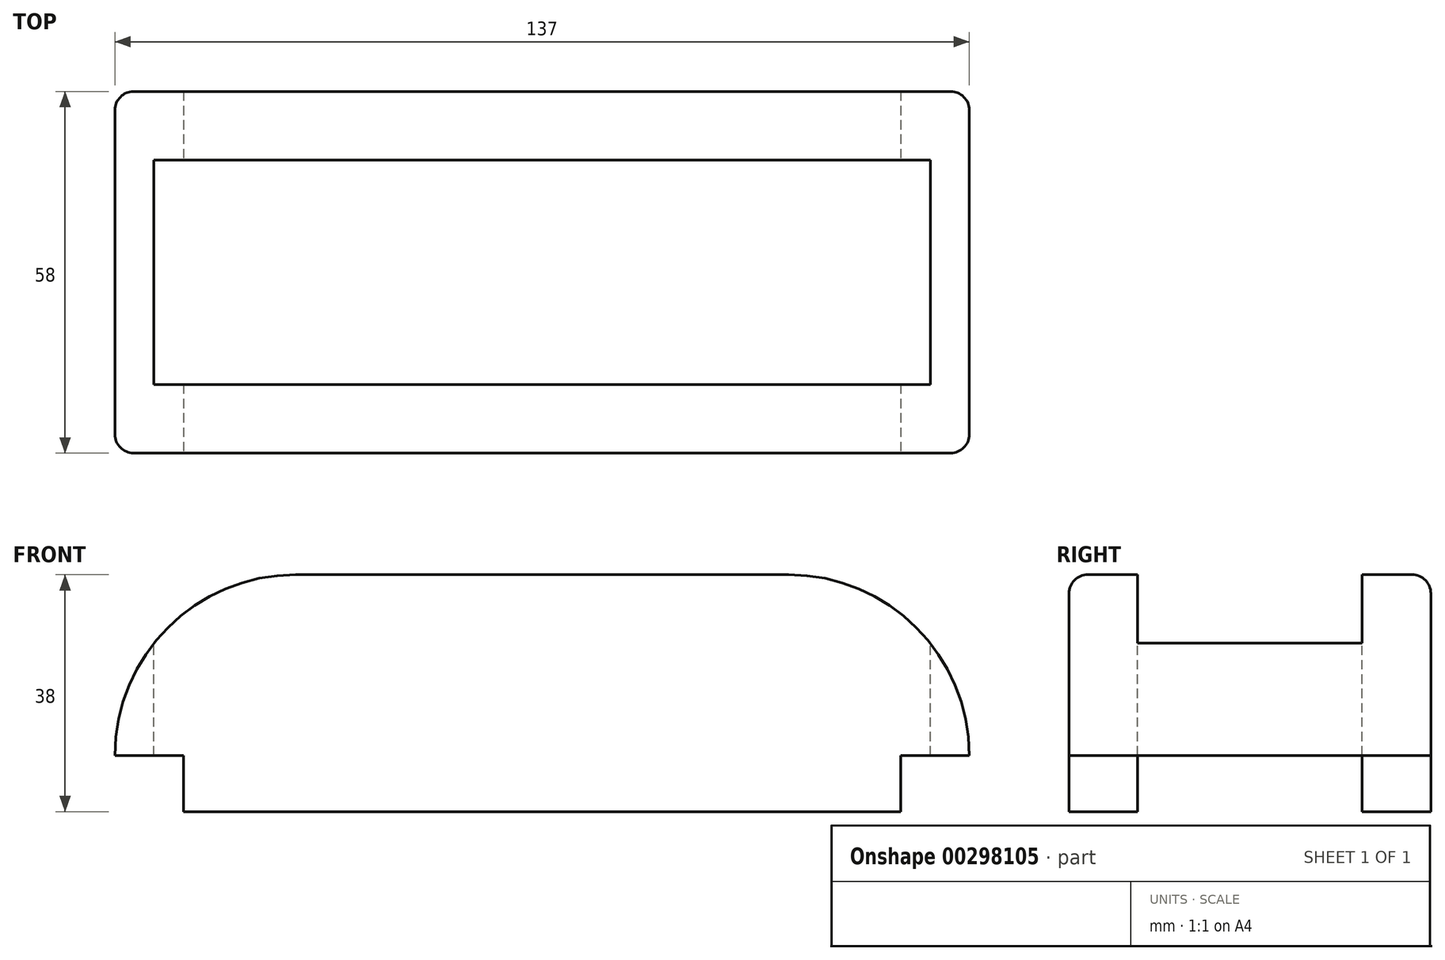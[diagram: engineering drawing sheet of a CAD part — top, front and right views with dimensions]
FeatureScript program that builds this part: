
annotation { "Feature Type Name" : "Feature", "Feature Type Description" : "" }
export const myFeature = defineFeature(function(context is Context, id is Id, definition is map)
    precondition{}
    {
        {
            var Q0;
            Q0=qCreatedBy(makeId("Front.planeOp"),FACE);
            var sketch = newSketch(context, id + "F0", { "sketchPlane" : qUnion([Q0])});
            skLineSegment(sketch, "E0.bottom", {"start": v(0, 0) * mm, "end": v(137, 0) * mm});
            skLineSegment(sketch, "E0.top", {"start": v(0, -38) * mm, "end": v(137, -38) * mm});
            skLineSegment(sketch, "E0.left", {"start": v(0, 0) * mm, "end": v(0, -38) * mm});
            skLineSegment(sketch, "E0.right", {"start": v(137, 0) * mm, "end": v(137, -38) * mm});
            skSolve(sketch);
        }
        {
            var Q0;
            Q0=makeQuery(id+"F0.imprint","IMPRINT",FACE,{"disambiguationData":[TD([[makeQuery(id+"F0.imprint","IMPRINT",EDGE,{"derivedFrom":sQuery(id+"F0.wireOp",EDGE,"E0.bottom")}),-1.0]])]});
            extrude(context, id + "F1", {"entities" : qUnion([Q0]), "depth" : 58 * mm});
        }
        {
            var Q0;
            Q0=makeQuery(id+"F1.opExtrude","CAP_FACE",FACE,{"disambiguationData":[OSD([sQuery(id+"F0.wireOp",EDGE,"E0.bottom"),sQuery(id+"F0.wireOp",EDGE,"E0.top"),sQuery(id+"F0.wireOp",EDGE,"E0.left"),sQuery(id+"F0.wireOp",EDGE,"E0.right")])],"isStart":false});
            var sketch = newSketch(context, id + "F2", { "sketchPlane" : qUnion([Q0])});
            skLineSegment(sketch, "E1.bottom", {"start": v(137, -38) * mm, "end": v(126, -38) * mm});
            skLineSegment(sketch, "E1.top", {"start": v(137, -29) * mm, "end": v(126, -29) * mm});
            skLineSegment(sketch, "E1.left", {"start": v(137, -38) * mm, "end": v(137, -29) * mm});
            skLineSegment(sketch, "E1.right", {"start": v(126, -38) * mm, "end": v(126, -29) * mm});
            skLineSegment(sketch, "E2.bottom", {"start": v(0, -38) * mm, "end": v(11, -38) * mm});
            skLineSegment(sketch, "E2.top", {"start": v(0, -29) * mm, "end": v(11, -29) * mm});
            skLineSegment(sketch, "E2.left", {"start": v(0, -38) * mm, "end": v(0, -29) * mm});
            skLineSegment(sketch, "E2.right", {"start": v(11, -38) * mm, "end": v(11, -29) * mm});
            skSolve(sketch);
        }
        {
            var Q0;
            Q0=makeQuery(id+"F2.imprint","IMPRINT",FACE,{"disambiguationData":[TD([[makeQuery(id+"F2.imprint","IMPRINT",EDGE,{"derivedFrom":sQuery(id+"F2.wireOp",EDGE,"E1.bottom")}),1.0]])]});
            var Q1;
            Q1=makeQuery(id+"F2.imprint","IMPRINT",FACE,{"disambiguationData":[TD([[makeQuery(id+"F2.imprint","IMPRINT",EDGE,{"derivedFrom":sQuery(id+"F2.wireOp",EDGE,"E2.bottom")}),1.0]])]});
            extrude(context, id + "F3", {"entities" : qUnion([Q0, Q1]), "operationType" : NewBodyOperationType.REMOVE, "endBound" : BoundingType.THROUGH_ALL, "oppositeDirection" : true, "depth" : 25 * mm});
        }
        {
            var Q0;
            Q0=makeQuery(id+"F1.opExtrude","SWEPT_EDGE",EDGE,{"disambiguationData":[OSD([sQuery(id+"F0.wireOp",EDGE,"E0.bottom"),sQuery(id+"F0.wireOp",EDGE,"E0.left")])]});
            var Q1;
            Q1=makeQuery(id+"F1.opExtrude","SWEPT_EDGE",EDGE,{"disambiguationData":[OSD([sQuery(id+"F0.wireOp",EDGE,"E0.bottom"),sQuery(id+"F0.wireOp",EDGE,"E0.right")])]});
            fillet(context, id + "F4", {"entities" : qUnion([Q0, Q1]), "radius" : 29 * mm, "tangentPropagation" : true, "allowEdgeOverflow" : false});
        }
        {
            var Q0;
            Q0=makeQuery(id+"F1.opExtrude","SWEPT_FACE",FACE,{"disambiguationData":[OSD([sQuery(id+"F0.wireOp",EDGE,"E0.bottom")])]});
            var sketch = newSketch(context, id + "F5", { "sketchPlane" : qUnion([Q0])});
            skLineSegment(sketch, "E3", {"start": v(29, -11) * mm, "end": v(140.01, -11) * mm});
            skLineSegment(sketch, "E4", {"start": v(29, -47) * mm, "end": v(140.01, -47) * mm});
            skLineSegment(sketch, "E5", {"start": v(29, -11) * mm, "end": v(-5.15, -11) * mm});
            skLineSegment(sketch, "E6", {"start": v(-5.15, -11) * mm, "end": v(-5.15, -47) * mm});
            skLineSegment(sketch, "E7", {"start": v(29, -47) * mm, "end": v(-5.15, -47) * mm});
            skLineSegment(sketch, "E8", {"start": v(140.01, -11) * mm, "end": v(140.01, -47) * mm});
            skSolve(sketch);
        }
        {
            var Q0;
            {var subQ0=sQuery(id+"F5.wireOp",EDGE,"E3");var subQ1=sQuery(id+"F0.wireOp",EDGE,"E0.bottom");var subQ2=makeQuery(id+"F1.opExtrude","SWEPT_FACE",FACE,{"disambiguationData":[OSD([subQ1])]});var subQ5=makeQuery(id+"F4.opFillet","BLEND_EDGE",EDGE,{"blendedFrom":[makeQuery(id+"F1.opExtrude","SWEPT_EDGE",EDGE,{"disambiguationData":[OSD([subQ1,sQuery(id+"F0.wireOp",EDGE,"E0.right")])]}),subQ2],"blendedInto":[subQ2]});var subQ6=makeQuery(id+"F5.imprint","INTERSECT",VERTEX,{"derivedFrom":[subQ5,subQ0]});Q0=makeQuery(id+"F5.imprint","IMPRINT",FACE,{"disambiguationData":[TD([[makeQuery(id+"F5.imprint","IMPRINT",EDGE,{"disambiguationData":[TD([[subQ6,1.0]])],"derivedFrom":subQ0}),-1.0]])]});}
            var Q1;
            {var subQ0=sQuery(id+"F5.wireOp",EDGE,"E5");Q1=makeQuery(id+"F5.imprint","IMPRINT",FACE,{"disambiguationData":[TD([[makeQuery(id+"F5.imprint","IMPRINT",EDGE,{"derivedFrom":subQ0}),1.0]])]});}
            var Q2;
            {var subQ0=sQuery(id+"F5.wireOp",EDGE,"E8");Q2=makeQuery(id+"F5.imprint","IMPRINT",FACE,{"disambiguationData":[TD([[makeQuery(id+"F5.imprint","IMPRINT",EDGE,{"derivedFrom":subQ0}),-1.0]])]});}
            extrude(context, id + "F6", {"entities" : qUnion([Q0, Q1, Q2]), "operationType" : NewBodyOperationType.REMOVE, "oppositeDirection" : true, "depth" : 11 * mm});
        }
        {
            var Q0;
            Q0=makeQuery(id+"F1.opExtrude","CAP_EDGE",EDGE,{"disambiguationData":[OSD([sQuery(id+"F0.wireOp",EDGE,"E0.bottom")])],"isStart":false});
            fillet(context, id + "F7", {"entities" : qUnion([Q0]), "radius" : 3 * mm, "tangentPropagation" : true, "allowEdgeOverflow" : false});
        }
        {
            var Q0;
            Q0=makeQuery(id+"F1.opExtrude","CAP_EDGE",EDGE,{"disambiguationData":[OSD([sQuery(id+"F0.wireOp",EDGE,"E0.bottom")])],"isStart":true});
            fillet(context, id + "F8", {"entities" : qUnion([Q0]), "radius" : 3 * mm, "tangentPropagation" : true, "allowEdgeOverflow" : false});
        }
        {
            var Q0;
            Q0=makeQuery(id+"F6.boolean.opBoolean","COPY",FACE,{"derivedFrom":makeQuery(id+"F6.opExtrude","CAP_FACE",FACE,{"disambiguationData":[OSD([sQuery(id+"F5.wireOp",EDGE,"E3"),sQuery(id+"F5.wireOp",EDGE,"E4"),sQuery(id+"F5.wireOp",EDGE,"E5"),sQuery(id+"F5.wireOp",EDGE,"E6"),sQuery(id+"F5.wireOp",EDGE,"E7"),sQuery(id+"F5.wireOp",EDGE,"E8")])],"isStart":false})});
            var sketch = newSketch(context, id + "F9", { "sketchPlane" : qUnion([Q0])});
            skLineSegment(sketch, "E9", {"start": v(112, -21.5) * mm, "end": v(99, -21.5) * mm});
            skLineSegment(sketch, "E10", {"start": v(112, -34.5) * mm, "end": v(99, -34.5) * mm});
            skArc(sketch, "E11", {"start": v(112, -21.5) * mm, "mid": v(118.5, -28) * mm, "end": v(112, -34.5) * mm});
            skArc(sketch, "E12.MirrorCS", {"start": v(25, -21.5) * mm, "mid": v(18.5, -28) * mm, "end": v(25, -34.5) * mm});
            skLineSegment(sketch, "E13.MirrorCS", {"start": v(25, -21.5) * mm, "end": v(38, -21.5) * mm});
            skLineSegment(sketch, "E14.MirrorCS", {"start": v(25, -34.5) * mm, "end": v(38, -34.5) * mm});
            skLineSegment(sketch, "E15", {"start": v(25, -21.5) * mm, "end": v(44, -21.5) * mm});
            skLineSegment(sketch, "E16", {"start": v(25, -34.5) * mm, "end": v(44, -34.5) * mm});
            skArc(sketch, "E17", {"start": v(44, -21.5) * mm, "mid": v(50.5, -28) * mm, "end": v(44, -34.5) * mm});
            skLineSegment(sketch, "E18", {"start": v(112, -21.5) * mm, "end": v(93, -21.5) * mm});
            skLineSegment(sketch, "E19", {"start": v(112, -34.5) * mm, "end": v(93, -34.5) * mm});
            skArc(sketch, "E20", {"start": v(93, -21.5) * mm, "mid": v(86.5, -28) * mm, "end": v(93, -34.5) * mm});
            skSolve(sketch);
        }
        {
            var Q0;
            Q0=makeQuery(id+"F9.imprint","IMPRINT",FACE,{"disambiguationData":[TD([[makeQuery(id+"F9.imprint","IMPRINT",EDGE,{"derivedFrom":sQuery(id+"F9.wireOp",EDGE,"ecdd1aa1-88c4-43f9-a364-6576c187db440.MirrorCS")}),-1.0]])]});
            var Q1;
            Q1=makeQuery(id+"F9.imprint","IMPRINT",FACE,{"disambiguationData":[TD([[makeQuery(id+"F9.imprint","IMPRINT",EDGE,{"derivedFrom":sQuery(id+"F9.wireOp",EDGE,"E9")}),1.0]])]});
            extrude(context, id + "F10", {"entities" : qUnion([Q0, Q1]), "operationType" : NewBodyOperationType.REMOVE, "endBound" : BoundingType.THROUGH_ALL, "oppositeDirection" : true, "depth" : 25 * mm});
        }
        {
            var Q0;
            {var subQ1=sQuery(id+"F9.wireOp",EDGE,"E11");Q0=makeQuery(id+"F9.imprint","IMPRINT",FACE,{"disambiguationData":[TD([[makeQuery(id+"F9.imprint","IMPRINT",EDGE,{"derivedFrom":subQ1}),-1.0]])]});}
            var Q1;
            {var subQ1=sQuery(id+"F9.wireOp",EDGE,"E12.MirrorCS");Q1=makeQuery(id+"F9.imprint","IMPRINT",FACE,{"disambiguationData":[TD([[makeQuery(id+"F9.imprint","IMPRINT",EDGE,{"derivedFrom":subQ1}),1.0]])]});}
            extrude(context, id + "F11", {"entities" : qUnion([Q0, Q1]), "operationType" : NewBodyOperationType.REMOVE, "endBound" : BoundingType.THROUGH_ALL, "oppositeDirection" : true, "depth" : 25 * mm});
        }
    });
